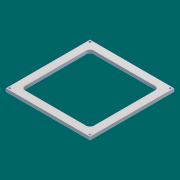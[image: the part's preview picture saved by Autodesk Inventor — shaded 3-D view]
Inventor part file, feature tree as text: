
AUTODESK INVENTOR PART (.ipt)
format: ipt  version: 2016 (Build 200138000, 138)  size: 104,960 bytes
history: native  units: mm
features: mirror x2, sketch x2, extrude x1, hole x1, fillet x1, projected_geometry x1
ambient origin geometry x8: Origin, YZ Plane, XZ Plane, XY Plane, X Axis, Y Axis, Z Axis, Center Point
bodies: Solid1 (feature_tree)
feature tree (8):
  extrude  "Extrusion1"  Depth=127.0mm
  hole  "Hole1"  [1 undecoded]
  mirror  "Mirror1"
  mirror  "Mirror2"
  fillet  "Fillet1"  Radius=5.08mm
  sketch  "Sketch1"  dims[d0=127.0mm d1=127.0mm]
  sketch  "Sketch2"  dims[d2=6.35mm d3=6.35mm d4=5.08mm d5=0.0mm d6=3.175mm d7=3.175mm d8=3.264mm d9=6.0mm d10=5.715mm d11=2.0mm d12=14.3117mm d13=8.0mm d14=20.594885mm d15=6.35mm]
  projected_geometry  "Projected Loop1"
note: 1 required parameter value undecoded (feature->parameter linkage not recoverable at this tier; creation-order binding heuristic only, values carry confidence <= 0.55)
